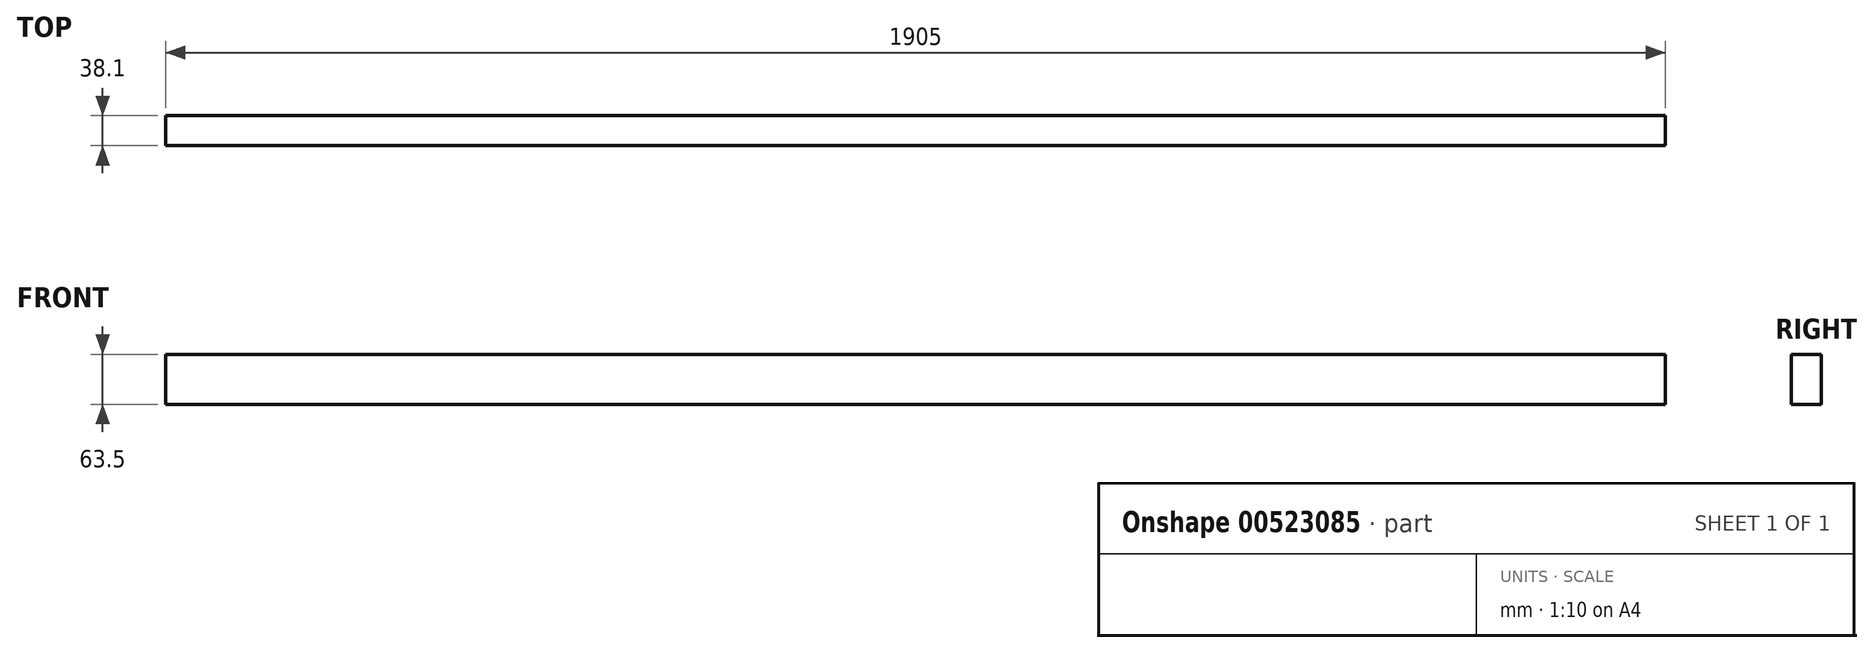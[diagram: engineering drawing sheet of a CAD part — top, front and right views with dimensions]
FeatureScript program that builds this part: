
annotation { "Feature Type Name" : "Feature", "Feature Type Description" : "" }
export const myFeature = defineFeature(function(context is Context, id is Id, definition is map)
    precondition{}
    {
        {
            var Q0;
            Q0=qCreatedBy(makeId("Top.planeOp"),FACE);
            var sketch = newSketch(context, id + "F0", { "sketchPlane" : qUnion([Q0])});
            skLineSegment(sketch, "E0.bottom", {"start": v(0, 0) * mm, "end": v(1905, 0) * mm});
            skLineSegment(sketch, "E0.top", {"start": v(0, 38.1) * mm, "end": v(1905, 38.1) * mm});
            skLineSegment(sketch, "E0.left", {"start": v(0, 0) * mm, "end": v(0, 38.1) * mm});
            skLineSegment(sketch, "E0.right", {"start": v(1905, 0) * mm, "end": v(1905, 38.1) * mm});
            skSolve(sketch);
        }
        {
            var Q0;
            Q0 = qSketchRegion(id + "F0", true);
            extrude(context, id + "F1", {"entities" : qUnion([Q0]), "depth" : 63.5 * mm, "offsetDistance" : 25.4 * mm});
        }
    });
